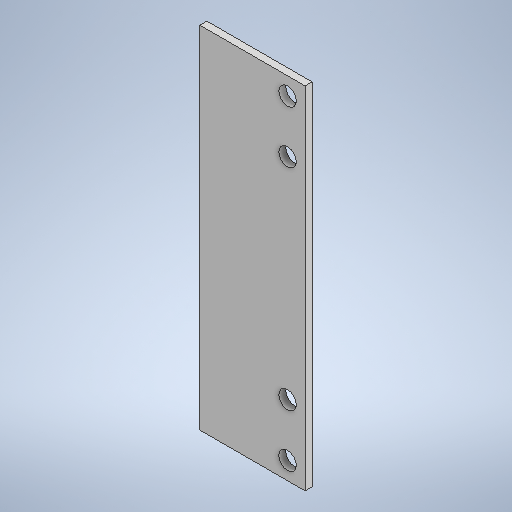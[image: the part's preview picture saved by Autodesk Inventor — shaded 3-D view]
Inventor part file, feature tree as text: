
AUTODESK INVENTOR PART (.ipt)
format: ipt  version: 2025 (Build 290162010, 162A)  size: 266,240 bytes
history: native  units: mm
features: sketch x2, sheet_metal_op x1, hole x1, other x1, projected_geometry x1
ambient origin geometry x8: Origin, YZ Plane, XZ Plane, XY Plane, X Axis, Y Axis, Z Axis, Center Point
bodies: Solid1 (feature_tree)
feature tree (6):
  sheet_metal_op  "Face1"
  hole  "Hole1"  [1 undecoded]
  sketch  "Sketch1"  dims[d2=8.0mm]
  other  "Plate1"
  sketch  "Sketch2"  dims[d3=20.0mm d4=6.0mm d5=4.0mm d6=2.0mm d7=90.0deg d8=8.0mm d9=20.594885mm d16=120.0mm d17=400.0mm d19=20.0mm d20=20.0mm d21=360.0mm d22=120.0mm d23=120.0mm]
  projected_geometry  "Projected Loop1"
note: 1 required parameter value undecoded (feature->parameter linkage not recoverable at this tier; creation-order binding heuristic only, values carry confidence <= 0.55)
